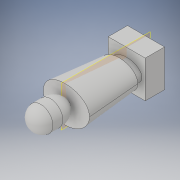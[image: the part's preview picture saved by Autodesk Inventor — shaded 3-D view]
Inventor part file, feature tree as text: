
AUTODESK INVENTOR PART (.ipt)
format: ipt  version: 2017 (Build 210142000, 142)  size: 255,488 bytes
history: native  units: in
note: dims shown in document units (in); Inventor stores cm internally (conversion verified against a paired STEP export)
features: sketch x5, extrude x4, projected_geometry x3, plane x1, revolve x1
ambient origin geometry x8: Origin, YZ Plane, XZ Plane, XY Plane, X Axis, Y Axis, Z Axis, Center Point
bodies: Solid1 (feature_tree)
feature tree (14):
  extrude  "Extrusion1"  Depth=0.575in
  extrude  "Extrusion2"  Depth=0.236in
  extrude  "Extrusion3"  Depth=0.115in TaperAngle=0.0deg
  plane  "Work Plane1"
  extrude  "Extrusion4"  Depth=0.84in
  revolve  "Revolution1"  Angle=90.0deg
  sketch  "Sketch1"  dims[d0=0.575in d1=0.575in]
  sketch  "Sketch2"  dims[d2=0.3in d3=0.0in d4=0.236in]
  sketch  "Sketch3"  dims[d5=0.155in d6=0.115in d7=0.0in]
  sketch  "Sketch4"  dims[d8=0.05in d9=0.84in d10=0.0344in]
  projected_geometry  "Projected Loop1"
  projected_geometry  "Projected Loop2"
  sketch  "Sketch5"  dims[d12=0.84in d13=0.0in d17=90.0deg]
  projected_geometry  "Projected Loop3"
